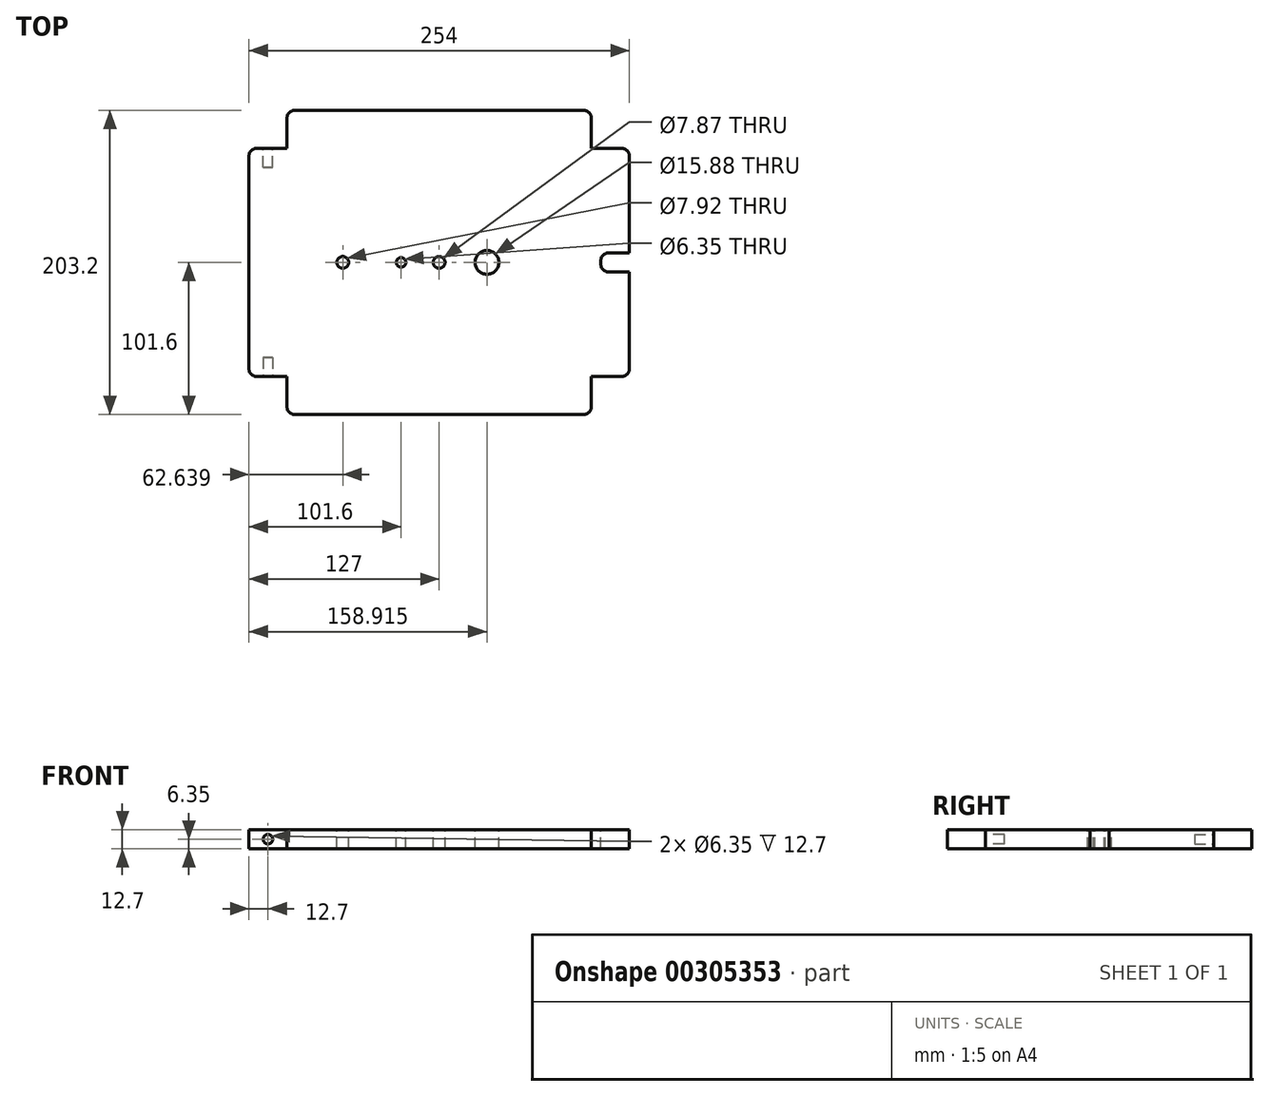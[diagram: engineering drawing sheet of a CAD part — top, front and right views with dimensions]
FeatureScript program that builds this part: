
annotation { "Feature Type Name" : "Feature", "Feature Type Description" : "" }
export const myFeature = defineFeature(function(context is Context, id is Id, definition is map)
    precondition{}
    {
        {
            var Q0;
            Q0=qCreatedBy(makeId("Top.planeOp"),FACE);
            var sketch = newSketch(context, id + "F0", { "sketchPlane" : qUnion([Q0])});
            skLineSegment(sketch, "E0.bottom", {"start": v(-127, 76.2) * mm, "end": v(127, 76.2) * mm});
            skLineSegment(sketch, "E0.top", {"start": v(-127, -76.2) * mm, "end": v(127, -76.2) * mm});
            skLineSegment(sketch, "E0.left", {"start": v(-127, 76.2) * mm, "end": v(-127, -76.2) * mm});
            skLineSegment(sketch, "E0.right", {"start": v(127, 76.2) * mm, "end": v(127, -76.2) * mm});
            skPoint(sketch, "E0.middle", {"position": v(0, 0) * mm});
            skSolve(sketch);
        }
        {
            var Q0;
            Q0=makeQuery(id+"F0.imprint","IMPRINT",FACE,{"disambiguationData":[TD([[makeQuery(id+"F0.imprint","IMPRINT",EDGE,{"derivedFrom":sQuery(id+"F0.wireOp",EDGE,"E0.bottom")}),-1.0]])]});
            extrude(context, id + "F1", {"entities" : qUnion([Q0]), "depth" : 12.7 * mm});
        }
        {
            var Q0;
            Q0=makeQuery(id+"F1.opExtrude","SWEPT_FACE",FACE,{"disambiguationData":[OSD([sQuery(id+"F0.wireOp",EDGE,"E0.bottom")])]});
            var sketch = newSketch(context, id + "F2", { "sketchPlane" : qUnion([Q0])});
            skLineSegment(sketch, "E1.bottom", {"start": v(-101.6, 12.7) * mm, "end": v(101.6, 12.7) * mm});
            skLineSegment(sketch, "E1.top", {"start": v(-101.6, 0) * mm, "end": v(101.6, 0) * mm});
            skLineSegment(sketch, "E1.left", {"start": v(-101.6, 12.7) * mm, "end": v(-101.6, 0) * mm});
            skLineSegment(sketch, "E1.right", {"start": v(101.6, 12.7) * mm, "end": v(101.6, 0) * mm});
            skPoint(sketch, "E1.middle", {"position": v(0, 6.35) * mm});
            skPoint(sketch, "E1.middle.positionSnap0", {"position": v(-127, 6.35) * mm});
            skPoint(sketch, "E1.middle.positionSnap1", {"position": v(0, 0) * mm});
            skPoint(sketch, "E1.centerSnap0", {"position": v(-127, 6.35) * mm});
            skPoint(sketch, "E1.centerSnap1", {"position": v(0, 0) * mm});
            skSolve(sketch);
        }
        {
            var Q0;
            Q0=makeQuery(id+"F2.imprint","IMPRINT",FACE,{"disambiguationData":[TD([[makeQuery(id+"F2.imprint","IMPRINT",EDGE,{"derivedFrom":sQuery(id+"F2.wireOp",EDGE,"E1.bottom")}),1.0]])]});
            extrude(context, id + "F3", {"entities" : qUnion([Q0]), "operationType" : NewBodyOperationType.ADD, "depth" : 25.4 * mm});
        }
        {
            var Q0;
            Q0=makeQuery(id+"F1.opExtrude","SWEPT_FACE",FACE,{"disambiguationData":[OSD([sQuery(id+"F0.wireOp",EDGE,"E0.top")])]});
            var sketch = newSketch(context, id + "F4", { "sketchPlane" : qUnion([Q0])});
            skLineSegment(sketch, "E2.bottom", {"start": v(-101.6, 12.7) * mm, "end": v(101.6, 12.7) * mm});
            skLineSegment(sketch, "E2.top", {"start": v(-101.6, 0) * mm, "end": v(101.6, 0) * mm});
            skLineSegment(sketch, "E2.left", {"start": v(-101.6, 12.7) * mm, "end": v(-101.6, 0) * mm});
            skLineSegment(sketch, "E2.right", {"start": v(101.6, 12.7) * mm, "end": v(101.6, 0) * mm});
            skPoint(sketch, "E2.middle", {"position": v(0, 6.35) * mm});
            skPoint(sketch, "E2.middle.positionSnap0", {"position": v(0, 0) * mm});
            skPoint(sketch, "E2.middle.positionSnap1", {"position": v(-127, 6.35) * mm});
            skPoint(sketch, "E2.centerSnap0", {"position": v(0, 0) * mm});
            skPoint(sketch, "E2.centerSnap1", {"position": v(-127, 6.35) * mm});
            skSolve(sketch);
        }
        {
            var Q0;
            Q0=makeQuery(id+"F4.imprint","IMPRINT",FACE,{"disambiguationData":[TD([[makeQuery(id+"F4.imprint","IMPRINT",EDGE,{"derivedFrom":sQuery(id+"F4.wireOp",EDGE,"E2.bottom")}),-1.0]])]});
            extrude(context, id + "F5", {"entities" : qUnion([Q0]), "operationType" : NewBodyOperationType.ADD, "depth" : 25.4 * mm});
        }
        {
            var Q0;
            {var subQ1=sQuery(id+"F0.wireOp",EDGE,"E0.left");var subQ2=sQuery(id+"F0.wireOp",EDGE,"E0.top");Q0=makeQuery(id+"F5.boolean.opBoolean","SPLIT",FACE,{"disambiguationData":[TD([makeQuery(id+"F1.opExtrude","SWEPT_FACE",FACE,{"disambiguationData":[OSD([subQ1])]})])],"derivedFrom":makeQuery(id+"F1.opExtrude","SWEPT_FACE",FACE,{"disambiguationData":[OSD([subQ2])]})});}
            var sketch = newSketch(context, id + "F6", { "sketchPlane" : qUnion([Q0])});
            skCircle(sketch, "E3", {"center": v(-114.3, 6.35) * mm, "radius": 3.18 * mm});
            skPoint(sketch, "E3.centerSnap0", {"position": v(-101.6, 6.35) * mm});
            skPoint(sketch, "E3.centerSnap1", {"position": v(-114.3, 12.7) * mm});
            skSolve(sketch);
        }
        {
            var Q0;
            Q0=makeQuery(id+"F6.imprint","IMPRINT",FACE,{"disambiguationData":[TD([[makeQuery(id+"F6.imprint","IMPRINT",EDGE,{"derivedFrom":sQuery(id+"F6.wireOp",EDGE,"E3")}),1.0]])]});
            extrude(context, id + "F7", {"entities" : qUnion([Q0]), "operationType" : NewBodyOperationType.REMOVE, "oppositeDirection" : true, "depth" : 12.7 * mm});
        }
        {
            var Q0;
            {var subQ1=sQuery(id+"F0.wireOp",EDGE,"E0.left");var subQ3=sQuery(id+"F0.wireOp",EDGE,"E0.bottom");Q0=makeQuery(id+"F3.boolean.opBoolean","SPLIT",FACE,{"disambiguationData":[TD([makeQuery(id+"F1.opExtrude","SWEPT_FACE",FACE,{"disambiguationData":[OSD([subQ1])]})])],"derivedFrom":makeQuery(id+"F1.opExtrude","SWEPT_FACE",FACE,{"disambiguationData":[OSD([subQ3])]})});}
            var sketch = newSketch(context, id + "F8", { "sketchPlane" : qUnion([Q0])});
            skCircle(sketch, "E4", {"center": v(114.3, 6.35) * mm, "radius": 3.18 * mm});
            skPoint(sketch, "E4.centerSnap0", {"position": v(127, 6.35) * mm});
            skPoint(sketch, "E4.centerSnap1", {"position": v(114.3, 12.7) * mm});
            skSolve(sketch);
        }
        {
            var Q0;
            Q0=makeQuery(id+"F8.imprint","IMPRINT",FACE,{"disambiguationData":[TD([[makeQuery(id+"F8.imprint","IMPRINT",EDGE,{"derivedFrom":sQuery(id+"F8.wireOp",EDGE,"E4")}),1.0]])]});
            extrude(context, id + "F9", {"entities" : qUnion([Q0]), "operationType" : NewBodyOperationType.REMOVE, "oppositeDirection" : true, "depth" : 12.7 * mm});
        }
        {
            var Q0;
            Q0=makeQuery(id+"F5.boolean.opBoolean","MERGE",FACE,{"derivedFrom":[makeQuery(id+"F3.boolean.opBoolean","MERGE",FACE,{"derivedFrom":[makeQuery(id+"F1.opExtrude","CAP_FACE",FACE,{"disambiguationData":[OSD([sQuery(id+"F0.wireOp",EDGE,"E0.bottom"),sQuery(id+"F0.wireOp",EDGE,"E0.top"),sQuery(id+"F0.wireOp",EDGE,"E0.left"),sQuery(id+"F0.wireOp",EDGE,"E0.right")])],"isStart":false}),makeQuery(id+"F3.opExtrude","SWEPT_FACE",FACE,{"disambiguationData":[OSD([sQuery(id+"F2.wireOp",EDGE,"E1.bottom")])]})]}),makeQuery(id+"F5.opExtrude","SWEPT_FACE",FACE,{"disambiguationData":[OSD([sQuery(id+"F4.wireOp",EDGE,"E2.bottom")])]})]});
            var sketch = newSketch(context, id + "F10", { "sketchPlane" : qUnion([Q0])});
            skLineSegment(sketch, "E5.bottom", {"start": v(127, 6.35) * mm, "end": v(107.95, 6.35) * mm});
            skLineSegment(sketch, "E5.top", {"start": v(127, -6.35) * mm, "end": v(107.95, -6.35) * mm});
            skLineSegment(sketch, "E5.left", {"start": v(127, 6.35) * mm, "end": v(127, -6.35) * mm});
            skLineSegment(sketch, "E5.right", {"start": v(107.95, 6.35) * mm, "end": v(107.95, -6.35) * mm});
            skSolve(sketch);
        }
        {
            var Q0;
            Q0=makeQuery(id+"F10.imprint","IMPRINT",FACE,{"disambiguationData":[TD([[makeQuery(id+"F10.imprint","IMPRINT",EDGE,{"derivedFrom":sQuery(id+"F10.wireOp",EDGE,"E5.bottom")}),1.0]])]});
            extrude(context, id + "F11", {"entities" : qUnion([Q0]), "operationType" : NewBodyOperationType.REMOVE, "oppositeDirection" : true, "depth" : 25.4 * mm});
        }
        {
            var Q0;
            Q0=makeQuery(id+"F5.opExtrude","CAP_EDGE",EDGE,{"disambiguationData":[OSD([sQuery(id+"F4.wireOp",EDGE,"E2.right")])],"isStart":false});
            var Q1;
            Q1=makeQuery(id+"F1.opExtrude","SWEPT_EDGE",EDGE,{"disambiguationData":[OSD([sQuery(id+"F0.wireOp",EDGE,"E0.top"),sQuery(id+"F0.wireOp",EDGE,"E0.right")])]});
            var Q2;
            Q2=makeQuery(id+"F11.boolean.opBoolean","COPY",EDGE,{"derivedFrom":makeQuery(id+"F11.opExtrude","SWEPT_EDGE",EDGE,{"disambiguationData":[OSD([sQuery(id+"F0.wireOp",EDGE,"E0.right"),sQuery(id+"F10.wireOp",EDGE,"E5.top"),sQuery(id+"F10.wireOp",EDGE,"E5.left")])]})});
            var Q3;
            Q3=makeQuery(id+"F11.boolean.opBoolean","COPY",EDGE,{"derivedFrom":makeQuery(id+"F11.opExtrude","SWEPT_EDGE",EDGE,{"disambiguationData":[OSD([sQuery(id+"F0.wireOp",EDGE,"E0.right"),sQuery(id+"F10.wireOp",EDGE,"E5.bottom"),sQuery(id+"F10.wireOp",EDGE,"E5.left")])]})});
            var Q4;
            Q4=makeQuery(id+"F11.boolean.opBoolean","COPY",EDGE,{"derivedFrom":makeQuery(id+"F11.opExtrude","SWEPT_EDGE",EDGE,{"disambiguationData":[OSD([sQuery(id+"F10.wireOp",EDGE,"E5.bottom"),sQuery(id+"F10.wireOp",EDGE,"E5.right")])]})});
            var Q5;
            Q5=makeQuery(id+"F11.boolean.opBoolean","COPY",EDGE,{"derivedFrom":makeQuery(id+"F11.opExtrude","SWEPT_EDGE",EDGE,{"disambiguationData":[OSD([sQuery(id+"F10.wireOp",EDGE,"E5.top"),sQuery(id+"F10.wireOp",EDGE,"E5.right")])]})});
            var Q6;
            Q6=makeQuery(id+"F1.opExtrude","SWEPT_EDGE",EDGE,{"disambiguationData":[OSD([sQuery(id+"F0.wireOp",EDGE,"E0.bottom"),sQuery(id+"F0.wireOp",EDGE,"E0.right")])]});
            var Q7;
            Q7=makeQuery(id+"F3.opExtrude","CAP_EDGE",EDGE,{"disambiguationData":[OSD([sQuery(id+"F2.wireOp",EDGE,"E1.left")])],"isStart":true});
            var Q8;
            Q8=makeQuery(id+"F3.opExtrude","CAP_EDGE",EDGE,{"disambiguationData":[OSD([sQuery(id+"F2.wireOp",EDGE,"E1.left")])],"isStart":false});
            var Q9;
            Q9=makeQuery(id+"F5.opExtrude","CAP_EDGE",EDGE,{"disambiguationData":[OSD([sQuery(id+"F4.wireOp",EDGE,"E2.right")])],"isStart":true});
            var Q10;
            Q10=makeQuery(id+"F5.opExtrude","CAP_EDGE",EDGE,{"disambiguationData":[OSD([sQuery(id+"F4.wireOp",EDGE,"E2.left")])],"isStart":false});
            var Q11;
            Q11=makeQuery(id+"F5.opExtrude","CAP_EDGE",EDGE,{"disambiguationData":[OSD([sQuery(id+"F4.wireOp",EDGE,"E2.left")])],"isStart":true});
            var Q12;
            Q12=makeQuery(id+"F1.opExtrude","SWEPT_EDGE",EDGE,{"disambiguationData":[OSD([sQuery(id+"F0.wireOp",EDGE,"E0.top"),sQuery(id+"F0.wireOp",EDGE,"E0.left")])]});
            var Q13;
            Q13=makeQuery(id+"F1.opExtrude","SWEPT_EDGE",EDGE,{"disambiguationData":[OSD([sQuery(id+"F0.wireOp",EDGE,"E0.bottom"),sQuery(id+"F0.wireOp",EDGE,"E0.left")])]});
            var Q14;
            Q14=makeQuery(id+"F3.opExtrude","CAP_EDGE",EDGE,{"disambiguationData":[OSD([sQuery(id+"F2.wireOp",EDGE,"E1.right")])],"isStart":true});
            var Q15;
            Q15=makeQuery(id+"F3.opExtrude","CAP_EDGE",EDGE,{"disambiguationData":[OSD([sQuery(id+"F2.wireOp",EDGE,"E1.right")])],"isStart":false});
            fillet(context, id + "F12", {"entities" : qUnion([Q0, Q1, Q2, Q3, Q4, Q5, Q6, Q7, Q8, Q9, Q10, Q11, Q12, Q13, Q14, Q15]), "radius" : 5.08 * mm, "tangentPropagation" : true, "allowEdgeOverflow" : false});
        }
        {
            var Q0;
            Q0=makeQuery(id+"F5.boolean.opBoolean","MERGE",FACE,{"derivedFrom":[makeQuery(id+"F3.boolean.opBoolean","MERGE",FACE,{"derivedFrom":[makeQuery(id+"F1.opExtrude","CAP_FACE",FACE,{"disambiguationData":[OSD([sQuery(id+"F0.wireOp",EDGE,"E0.bottom"),sQuery(id+"F0.wireOp",EDGE,"E0.top"),sQuery(id+"F0.wireOp",EDGE,"E0.left"),sQuery(id+"F0.wireOp",EDGE,"E0.right")])],"isStart":false}),makeQuery(id+"F3.opExtrude","SWEPT_FACE",FACE,{"disambiguationData":[OSD([sQuery(id+"F2.wireOp",EDGE,"E1.bottom")])]})]}),makeQuery(id+"F5.opExtrude","SWEPT_FACE",FACE,{"disambiguationData":[OSD([sQuery(id+"F4.wireOp",EDGE,"E2.bottom")])]})]});
            var sketch = newSketch(context, id + "F13", { "sketchPlane" : qUnion([Q0])});
            skCircle(sketch, "E6", {"center": v(0, 0) * mm, "radius": 3.94 * mm});
            skSolve(sketch);
        }
        {
            var Q0;
            Q0=makeQuery(id+"F13.imprint","IMPRINT",FACE,{"disambiguationData":[TD([[makeQuery(id+"F13.imprint","IMPRINT",EDGE,{"derivedFrom":sQuery(id+"F13.wireOp",EDGE,"E6")}),1.0]])]});
            extrude(context, id + "F14", {"entities" : qUnion([Q0]), "operationType" : NewBodyOperationType.REMOVE, "oppositeDirection" : true, "depth" : 25.4 * mm});
        }
        {
            var Q0;
            Q0=makeQuery(id+"F5.boolean.opBoolean","MERGE",FACE,{"derivedFrom":[makeQuery(id+"F3.boolean.opBoolean","MERGE",FACE,{"derivedFrom":[makeQuery(id+"F1.opExtrude","CAP_FACE",FACE,{"disambiguationData":[OSD([sQuery(id+"F0.wireOp",EDGE,"E0.bottom"),sQuery(id+"F0.wireOp",EDGE,"E0.top"),sQuery(id+"F0.wireOp",EDGE,"E0.left"),sQuery(id+"F0.wireOp",EDGE,"E0.right")])],"isStart":false}),makeQuery(id+"F3.opExtrude","SWEPT_FACE",FACE,{"disambiguationData":[OSD([sQuery(id+"F2.wireOp",EDGE,"E1.bottom")])]})]}),makeQuery(id+"F5.opExtrude","SWEPT_FACE",FACE,{"disambiguationData":[OSD([sQuery(id+"F4.wireOp",EDGE,"E2.bottom")])]})]});
            var sketch = newSketch(context, id + "F15", { "sketchPlane" : qUnion([Q0])});
            skCircle(sketch, "E7", {"center": v(31.92, 0) * mm, "radius": 7.94 * mm});
            skSolve(sketch);
        }
        {
            var Q0;
            Q0=makeQuery(id+"F15.imprint","IMPRINT",FACE,{"disambiguationData":[TD([[makeQuery(id+"F15.imprint","IMPRINT",EDGE,{"derivedFrom":sQuery(id+"F15.wireOp",EDGE,"E7")}),1.0]])]});
            extrude(context, id + "F16", {"entities" : qUnion([Q0]), "operationType" : NewBodyOperationType.REMOVE, "oppositeDirection" : true, "depth" : 25.4 * mm});
        }
        {
            var Q0;
            Q0=makeQuery(id+"F5.boolean.opBoolean","MERGE",FACE,{"derivedFrom":[makeQuery(id+"F3.boolean.opBoolean","MERGE",FACE,{"derivedFrom":[makeQuery(id+"F1.opExtrude","CAP_FACE",FACE,{"disambiguationData":[OSD([sQuery(id+"F0.wireOp",EDGE,"E0.bottom"),sQuery(id+"F0.wireOp",EDGE,"E0.top"),sQuery(id+"F0.wireOp",EDGE,"E0.left"),sQuery(id+"F0.wireOp",EDGE,"E0.right")])],"isStart":false}),makeQuery(id+"F3.opExtrude","SWEPT_FACE",FACE,{"disambiguationData":[OSD([sQuery(id+"F2.wireOp",EDGE,"E1.bottom")])]})]}),makeQuery(id+"F5.opExtrude","SWEPT_FACE",FACE,{"disambiguationData":[OSD([sQuery(id+"F4.wireOp",EDGE,"E2.bottom")])]})]});
            var sketch = newSketch(context, id + "F17", { "sketchPlane" : qUnion([Q0])});
            skCircle(sketch, "E8", {"center": v(-64.36, 0) * mm, "radius": 3.96 * mm});
            skSolve(sketch);
        }
        {
            var Q0;
            Q0=makeQuery(id+"F17.imprint","IMPRINT",FACE,{"disambiguationData":[TD([[makeQuery(id+"F17.imprint","IMPRINT",EDGE,{"derivedFrom":sQuery(id+"F17.wireOp",EDGE,"E8")}),1.0]])]});
            extrude(context, id + "F18", {"entities" : qUnion([Q0]), "operationType" : NewBodyOperationType.REMOVE, "oppositeDirection" : true, "depth" : 25.4 * mm});
        }
        {
            var Q0;
            Q0=makeQuery(id+"F5.boolean.opBoolean","MERGE",FACE,{"derivedFrom":[makeQuery(id+"F3.boolean.opBoolean","MERGE",FACE,{"derivedFrom":[makeQuery(id+"F1.opExtrude","CAP_FACE",FACE,{"disambiguationData":[OSD([sQuery(id+"F0.wireOp",EDGE,"E0.bottom"),sQuery(id+"F0.wireOp",EDGE,"E0.top"),sQuery(id+"F0.wireOp",EDGE,"E0.left"),sQuery(id+"F0.wireOp",EDGE,"E0.right")])],"isStart":false}),makeQuery(id+"F3.opExtrude","SWEPT_FACE",FACE,{"disambiguationData":[OSD([sQuery(id+"F2.wireOp",EDGE,"E1.bottom")])]})]}),makeQuery(id+"F5.opExtrude","SWEPT_FACE",FACE,{"disambiguationData":[OSD([sQuery(id+"F4.wireOp",EDGE,"E2.bottom")])]})]});
            var sketch = newSketch(context, id + "F19", { "sketchPlane" : qUnion([Q0])});
            skCircle(sketch, "E9", {"center": v(-25.4, 0) * mm, "radius": 3.18 * mm});
            skSolve(sketch);
        }
        {
            var Q0;
            Q0=makeQuery(id+"F19.imprint","IMPRINT",FACE,{"disambiguationData":[TD([[makeQuery(id+"F19.imprint","IMPRINT",EDGE,{"derivedFrom":sQuery(id+"F19.wireOp",EDGE,"E9")}),1.0]])]});
            extrude(context, id + "F20", {"entities" : qUnion([Q0]), "operationType" : NewBodyOperationType.REMOVE, "oppositeDirection" : true, "depth" : 25.4 * mm});
        }
    });
